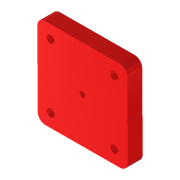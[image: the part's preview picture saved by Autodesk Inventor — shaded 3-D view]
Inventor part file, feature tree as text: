
AUTODESK INVENTOR PART (.ipt)
format: ipt  version: 2022 (Build 260153000, 153)  size: 181,760 bytes
history: native  units: mm
features: other x3, hole x1, sketch x1, projected_geometry x1
ambient origin geometry x8: Origin, YZ Plane, XZ Plane, XY Plane, X Axis, Y Axis, Z Axis, Center Point
bodies: Volumenkörper1 (feature_tree)
feature tree (6):
  other  "IM_Mold_plate.ipt"
  hole  "Bohrung1"  [1 undecoded]
  other  "Volumenkörper4::IM_Mold_plate.ipt"
  other  "Bezeichnung1"
  sketch  "Skizze1"  dims[d0=10.0mm d1=3.2mm d2=6.0mm d3=6.5mm d4=3.0mm d5=90.0deg d6=8.0mm d7=20.594885mm]
  projected_geometry  "Projizierte Kontur1"
note: 1 required parameter value undecoded (feature->parameter linkage not recoverable at this tier; creation-order binding heuristic only, values carry confidence <= 0.55)
